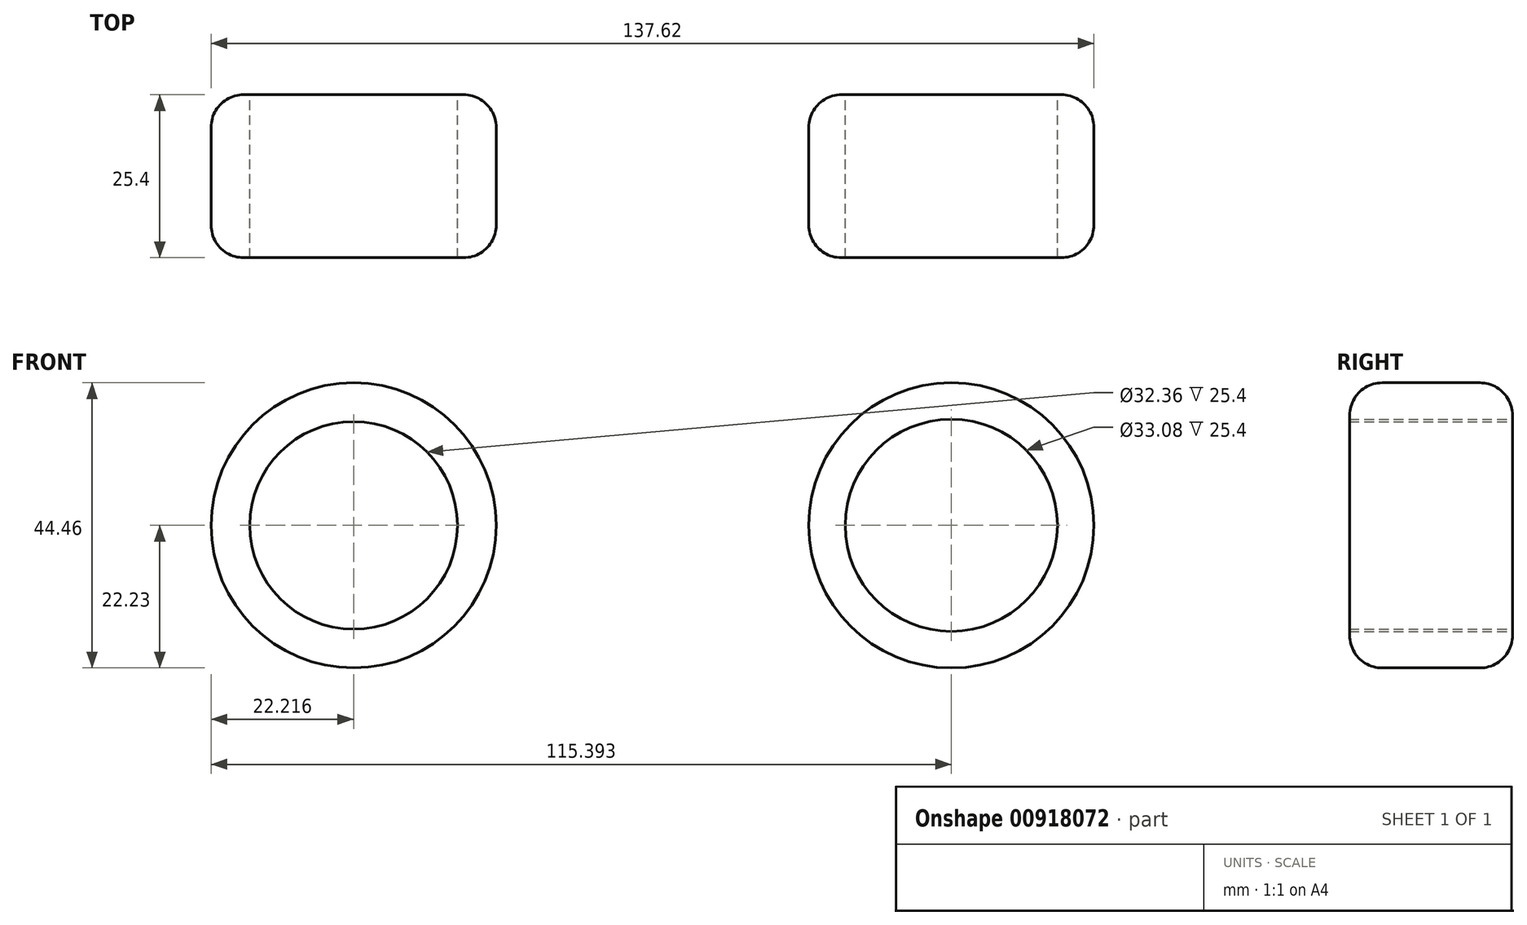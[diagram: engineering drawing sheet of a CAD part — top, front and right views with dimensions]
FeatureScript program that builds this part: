
annotation { "Feature Type Name" : "Feature", "Feature Type Description" : "" }
export const myFeature = defineFeature(function(context is Context, id is Id, definition is map)
    precondition{}
    {
        {
            var Q0;
            Q0=qCreatedBy(makeId("Front.planeOp"),FACE);
            var sketch = newSketch(context, id + "F0", { "sketchPlane" : qUnion([Q0])});
            skCircle(sketch, "E0", {"center": v(-73.55, 0) * mm, "radius": 22.22 * mm});
            skCircle(sketch, "E1", {"center": v(19.62, 0) * mm, "radius": 22.23 * mm});
            skCircle(sketch, "E2", {"center": v(-73.55, 0) * mm, "radius": 16.18 * mm});
            skCircle(sketch, "E3", {"center": v(19.62, 0) * mm, "radius": 16.54 * mm});
            skSolve(sketch);
        }
        {
            var Q0;
            Q0=makeQuery(id+"F0.imprint","IMPRINT",FACE,{"disambiguationData":[TD([[makeQuery(id+"F0.imprint","IMPRINT",EDGE,{"derivedFrom":sQuery(id+"F0.wireOp",EDGE,"E0")}),1.0]])]});
            var Q1;
            Q1=makeQuery(id+"F0.imprint","IMPRINT",FACE,{"disambiguationData":[TD([[makeQuery(id+"F0.imprint","IMPRINT",EDGE,{"derivedFrom":sQuery(id+"F0.wireOp",EDGE,"E1")}),1.0]])]});
            extrude(context, id + "F1", {"entities" : qUnion([Q0, Q1]), "depth" : 25.4 * mm, "offsetDistance" : 25.4 * mm});
        }
        {
            var Q0;
            Q0=makeQuery(id+"F1.opExtrude","CAP_EDGE",EDGE,{"disambiguationData":[OSD([sQuery(id+"F0.wireOp",EDGE,"E0")])],"isStart":false});
            var Q1;
            Q1=makeQuery(id+"F1.opExtrude","CAP_EDGE",EDGE,{"disambiguationData":[OSD([sQuery(id+"F0.wireOp",EDGE,"E0")])],"isStart":true});
            var Q2;
            Q2=makeQuery(id+"F1.opExtrude","CAP_EDGE",EDGE,{"disambiguationData":[OSD([sQuery(id+"F0.wireOp",EDGE,"E1")])],"isStart":true});
            var Q3;
            Q3=makeQuery(id+"F1.opExtrude","CAP_EDGE",EDGE,{"disambiguationData":[OSD([sQuery(id+"F0.wireOp",EDGE,"E1")])],"isStart":false});
            fillet(context, id + "F2", {"entities" : qUnion([Q0, Q1, Q2, Q3]), "radius" : 5.08 * mm, "tangentPropagation" : true, "allowEdgeOverflow" : false});
        }
    });
